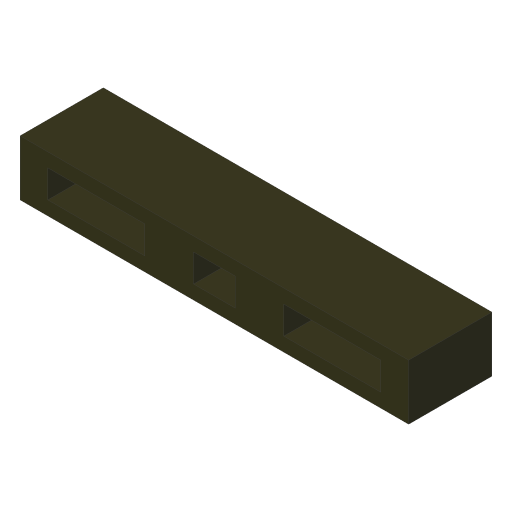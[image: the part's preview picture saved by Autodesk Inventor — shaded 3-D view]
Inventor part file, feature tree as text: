
AUTODESK INVENTOR PART (.ipt)
format: ipt  version: 2023.4 (Build 274418000, 418)  size: 241,664 bytes
history: native  units: in
note: dims shown in document units (in); Inventor stores cm internally (conversion verified against a paired STEP export)
features: extrude x1, sketch x1
ambient origin geometry x8: Origin, YZ Plane, XZ Plane, XY Plane, X Axis, Y Axis, Z Axis, Center Point
bodies: Solid1 (feature_tree)
feature tree (2):
  extrude  "Extrusion1"  Depth=0.1969in
  sketch  "Sketch1"  dims[d0=2.7559in d1=0.1969in d2=0.3937in d3=1.378in d5=0.1969in d6=0.1969in d7=0.1969in d8=0.689in d9=0.689in d10=0.0984in d11=0.5906in d12=0.0in d13=0.2953in d14=0.1969in d15=0.1476in d16=0.0984in]
